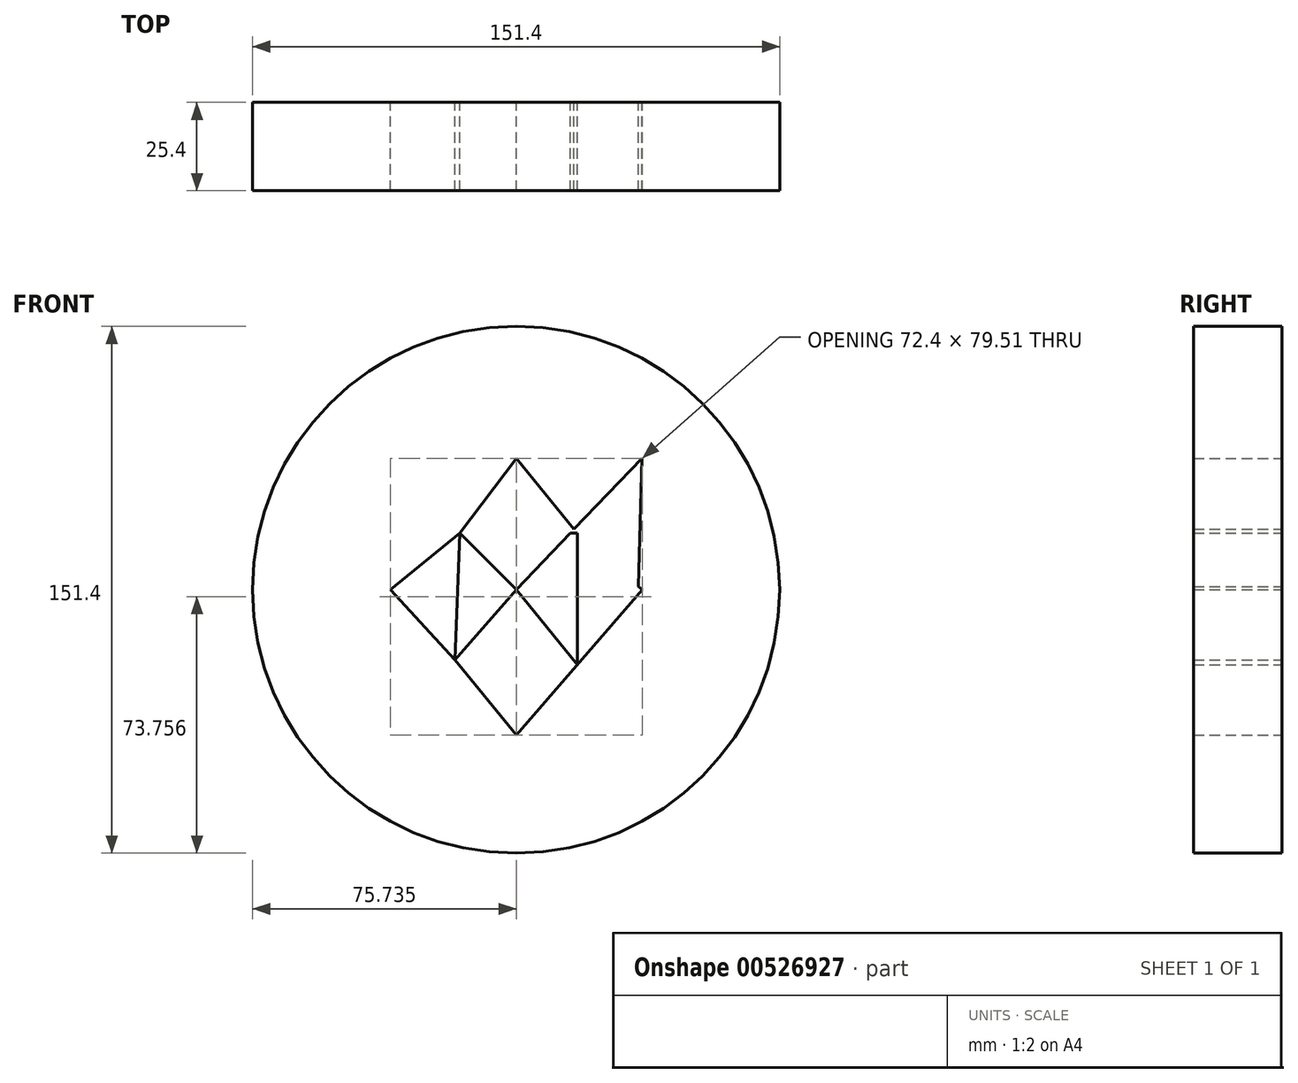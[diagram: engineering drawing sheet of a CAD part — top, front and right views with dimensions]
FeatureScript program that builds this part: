
annotation { "Feature Type Name" : "Feature", "Feature Type Description" : "" }
export const myFeature = defineFeature(function(context is Context, id is Id, definition is map)
    precondition{}
    {
        {
            var Q0;
            Q0=qCreatedBy(makeId("Front.planeOp"),FACE);
            var sketch = newSketch(context, id + "F0", { "sketchPlane" : qUnion([Q0])});
            skCircle(sketch, "E0", {"center": v(0, 0) * mm, "radius": 75.7 * mm});
            skLineSegment(sketch, "E1", {"start": v(0, -75.7) * mm, "end": v(-75.7, 0) * mm});
            skLineSegment(sketch, "E2", {"start": v(-75.7, 0) * mm, "end": v(-1.76, 73.94) * mm});
            skLineSegment(sketch, "E3", {"start": v(-1.76, 73.94) * mm, "end": v(75.7, 0) * mm});
            skLineSegment(sketch, "E4", {"start": v(75.7, 0) * mm, "end": v(0, -75.7) * mm});
            skLineSegment(sketch, "E5", {"start": v(34, -41.7) * mm, "end": v(0, 0) * mm});
            skLineSegment(sketch, "E6", {"start": v(0, 0) * mm, "end": v(36.1, 37.81) * mm});
            skLineSegment(sketch, "E7", {"start": v(36.1, 37.81) * mm, "end": v(0, 0) * mm});
            skLineSegment(sketch, "E8", {"start": v(0, 0) * mm, "end": v(-37.81, 37.81) * mm});
            skLineSegment(sketch, "E9", {"start": v(-37.81, 37.81) * mm, "end": v(0, 0) * mm});
            skLineSegment(sketch, "E10", {"start": v(0, 0) * mm, "end": v(-35.2, -40.5) * mm});
            skLineSegment(sketch, "E11", {"start": v(-35.2, -40.5) * mm, "end": v(34, -41.7) * mm});
            skLineSegment(sketch, "E12", {"start": v(34, -41.7) * mm, "end": v(36.1, 37.81) * mm});
            skLineSegment(sketch, "E13", {"start": v(36.1, 37.81) * mm, "end": v(-37.81, 37.81) * mm});
            skLineSegment(sketch, "E14", {"start": v(-35.94, 36.36) * mm, "end": v(-35.2, -40.5) * mm});
            skLineSegment(sketch, "E15", {"start": v(0, -41.7) * mm, "end": v(-17.54, -20.19) * mm});
            skLineSegment(sketch, "E16", {"start": v(-17.54, -20.19) * mm, "end": v(0, -41.7) * mm});
            skLineSegment(sketch, "E17", {"start": v(0, -41.7) * mm, "end": v(17.54, -21.51) * mm});
            skLineSegment(sketch, "E18", {"start": v(-17.54, -20.19) * mm, "end": v(17.54, -21.51) * mm});
            skLineSegment(sketch, "E19", {"start": v(17.54, -21.51) * mm, "end": v(36.24, 0) * mm});
            skLineSegment(sketch, "E20", {"start": v(36.24, 0) * mm, "end": v(17.54, 16.25) * mm});
            skLineSegment(sketch, "E21", {"start": v(17.54, 16.25) * mm, "end": v(17.54, -21.51) * mm});
            skLineSegment(sketch, "E22", {"start": v(17.54, 16.25) * mm, "end": v(0, 37.76) * mm});
            skLineSegment(sketch, "E23", {"start": v(0, 37.76) * mm, "end": v(-16.25, 16.25) * mm});
            skLineSegment(sketch, "E24", {"start": v(-16.25, 16.25) * mm, "end": v(17.54, 16.25) * mm});
            skLineSegment(sketch, "E25", {"start": v(-16.25, 16.25) * mm, "end": v(-36.17, 0) * mm});
            skLineSegment(sketch, "E26", {"start": v(-36.17, 0) * mm, "end": v(-17.54, -20.19) * mm});
            skLineSegment(sketch, "E27", {"start": v(-17.54, -20.19) * mm, "end": v(-16.25, 16.25) * mm});
            skSolve(sketch);
        }
        {
            var Q0;
            Q0 = qSketchRegion(id + "F0", true);
            var Q1;
            {var subQ0=sQuery(id+"F0.wireOp",EDGE,"E11");var subQ3=sQuery(id+"F0.wireOp",EDGE,"E16");var subQ5=makeQuery(id+"F0.imprint","INTERSECT",VERTEX,{"derivedFrom":[subQ0,subQ3]});Q1=makeQuery(id+"F0.imprint","IMPRINT",FACE,{"disambiguationData":[TD([[makeQuery(id+"F0.imprint","IMPRINT",EDGE,{"disambiguationData":[TD([[subQ5,1.0]])],"derivedFrom":subQ0}),1.0]])]});}
            var Q2;
            {var subQ0=sQuery(id+"F0.wireOp",EDGE,"E11");var subQ3=sQuery(id+"F0.wireOp",EDGE,"E17");var subQ5=makeQuery(id+"F0.imprint","INTERSECT",VERTEX,{"derivedFrom":[subQ0,subQ3]});Q2=makeQuery(id+"F0.imprint","IMPRINT",FACE,{"disambiguationData":[TD([[makeQuery(id+"F0.imprint","IMPRINT",EDGE,{"disambiguationData":[TD([[subQ5,-1.0]])],"derivedFrom":subQ0}),1.0]])]});}
            var Q3;
            {var subQ0=sQuery(id+"F0.wireOp",EDGE,"E13");Q3=makeQuery(id+"F0.imprint","IMPRINT",FACE,{"disambiguationData":[TD([[makeQuery(id+"F0.imprint","IMPRINT",EDGE,{"derivedFrom":subQ0}),1.0]])]});}
            var Q4;
            {var subQ0=sQuery(id+"F0.wireOp",EDGE,"E12");var subQ3=sQuery(id+"F0.wireOp",EDGE,"E19");var subQ5=makeQuery(id+"F0.imprint","INTERSECT",VERTEX,{"derivedFrom":[subQ0,subQ3]});Q4=makeQuery(id+"F0.imprint","IMPRINT",FACE,{"disambiguationData":[TD([[makeQuery(id+"F0.imprint","IMPRINT",EDGE,{"disambiguationData":[TD([[subQ5,1.0]])],"derivedFrom":subQ0}),1.0]])]});}
            var Q5;
            {var subQ1=sQuery(id+"F0.wireOp",EDGE,"E7");var subQ3=sQuery(id+"F0.wireOp",EDGE,"E22");var subQ4=makeQuery(id+"F0.imprint","INTERSECT",VERTEX,{"derivedFrom":[subQ1,subQ3]});Q5=makeQuery(id+"F0.imprint","IMPRINT",FACE,{"disambiguationData":[TD([[makeQuery(id+"F0.imprint","IMPRINT",EDGE,{"disambiguationData":[TD([[subQ4,1.0]])],"derivedFrom":subQ1}),1.0]])]});}
            var Q6;
            {var subQ1=sQuery(id+"F0.wireOp",EDGE,"E9");var subQ3=sQuery(id+"F0.wireOp",EDGE,"E14");var subQ4=makeQuery(id+"F0.imprint","INTERSECT",VERTEX,{"derivedFrom":[subQ1,subQ3]});Q6=makeQuery(id+"F0.imprint","IMPRINT",FACE,{"disambiguationData":[TD([[makeQuery(id+"F0.imprint","IMPRINT",EDGE,{"disambiguationData":[TD([[subQ4,-1.0]])],"derivedFrom":subQ3}),1.0]])]});}
            var Q7;
            {var subQ0=sQuery(id+"F0.wireOp",EDGE,"E14");var subQ3=sQuery(id+"F0.wireOp",EDGE,"E26");var subQ5=makeQuery(id+"F0.imprint","INTERSECT",VERTEX,{"derivedFrom":[subQ0,subQ3]});Q7=makeQuery(id+"F0.imprint","IMPRINT",FACE,{"disambiguationData":[TD([[makeQuery(id+"F0.imprint","IMPRINT",EDGE,{"disambiguationData":[TD([[subQ5,-1.0]])],"derivedFrom":subQ0}),1.0]])]});}
            var Q8;
            {var subQ3=sQuery(id+"F0.wireOp",EDGE,"E21");Q8=makeQuery(id+"F0.imprint","IMPRINT",FACE,{"disambiguationData":[TD([[makeQuery(id+"F0.imprint","IMPRINT",EDGE,{"derivedFrom":subQ3}),-1.0]])]});}
            var Q9;
            {var subQ3=sQuery(id+"F0.wireOp",EDGE,"E27");Q9=makeQuery(id+"F0.imprint","IMPRINT",FACE,{"disambiguationData":[TD([[makeQuery(id+"F0.imprint","IMPRINT",EDGE,{"derivedFrom":subQ3}),-1.0]])]});}
            extrude(context, id + "F1", {"entities" : qUnion([Q0, Q1, Q2, Q3, Q4, Q5, Q6, Q7, Q8, Q9]), "depth" : 25.4 * mm, "offsetDistance" : 25.4 * mm});
        }
    });
